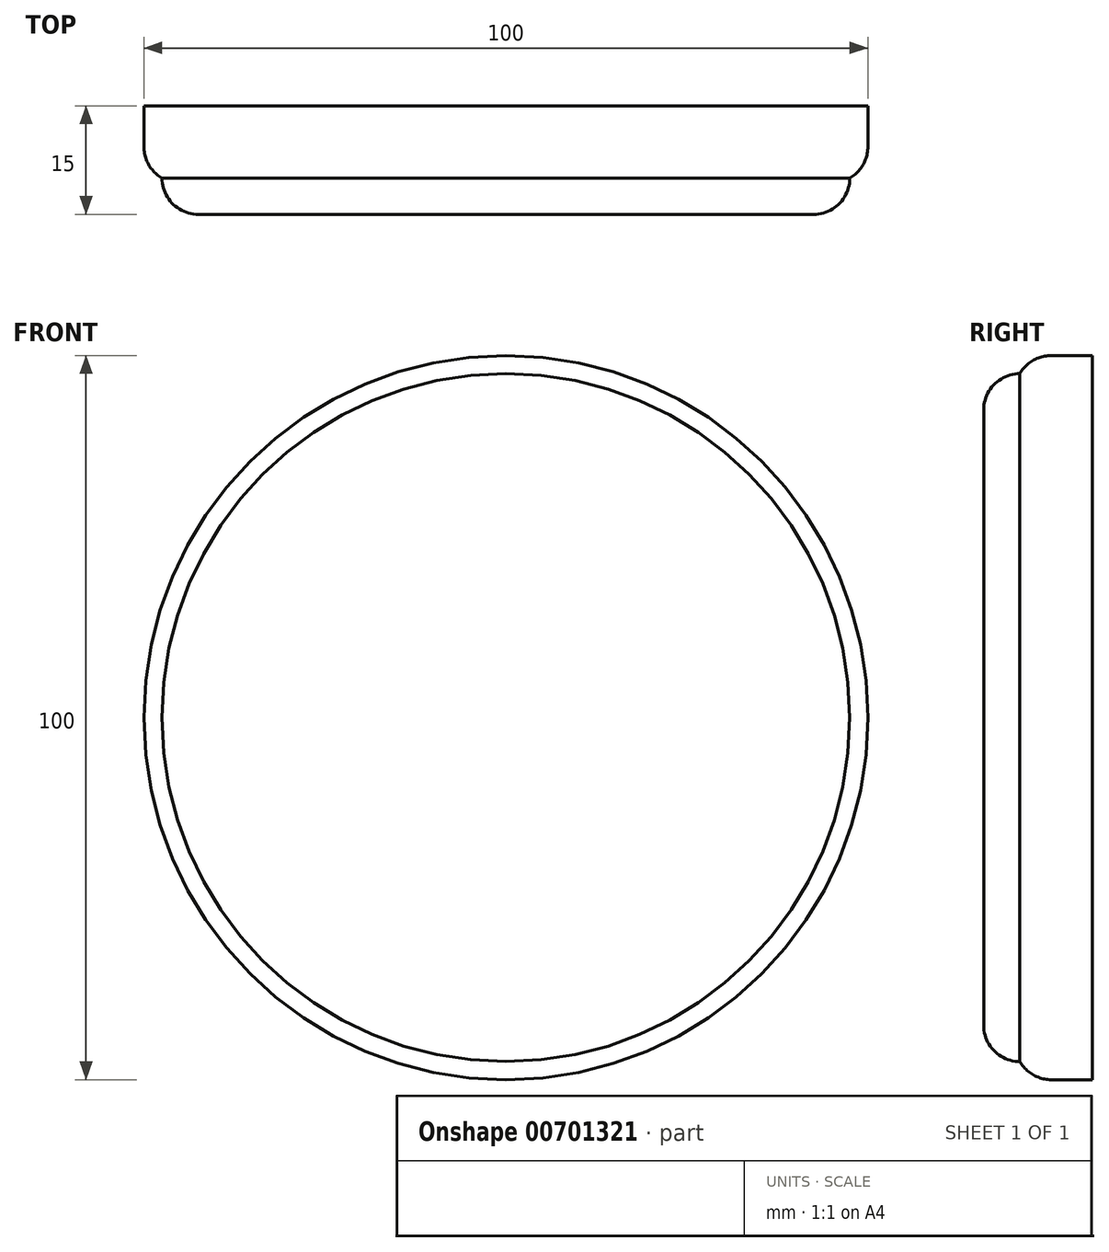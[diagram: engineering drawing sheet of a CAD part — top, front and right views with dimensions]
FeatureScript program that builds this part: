
annotation { "Feature Type Name" : "Feature", "Feature Type Description" : "" }
export const myFeature = defineFeature(function(context is Context, id is Id, definition is map)
    precondition{}
    {
        {
            var Q0;
            Q0=qCreatedBy(makeId("Front.planeOp"),FACE);
            var sketch = newSketch(context, id + "F0", { "sketchPlane" : qUnion([Q0])});
            skCircle(sketch, "E0", {"center": v(0, 0) * mm, "radius": 50 * mm});
            skSolve(sketch);
        }
        {
            var Q0;
            Q0 = qSketchRegion(id + "F0", true);
            extrude(context, id + "F1", {"entities" : qUnion([Q0]), "depth" : 10 * mm, "offsetDistance" : 25 * mm});
        }
        {
            var Q0;
            Q0=makeQuery(id+"F1.opExtrude","CAP_FACE",FACE,{"disambiguationData":[OSD([sQuery(id+"F0.wireOp",EDGE,"E0")])],"isStart":false});
            var sketch = newSketch(context, id + "F2", { "sketchPlane" : qUnion([Q0])});
            skCircle(sketch, "E1", {"center": v(0, 0) * mm, "radius": 47.5 * mm});
            skSolve(sketch);
        }
        {
            var Q0;
            Q0=makeQuery(id+"F2.imprint","IMPRINT",FACE,{"disambiguationData":[TD([[makeQuery(id+"F2.imprint","IMPRINT",EDGE,{"derivedFrom":sQuery(id+"F2.wireOp",EDGE,"E1")}),1.0]])]});
            extrude(context, id + "F3", {"entities" : qUnion([Q0]), "operationType" : NewBodyOperationType.ADD, "depth" : 5 * mm, "offsetDistance" : 25 * mm});
        }
        {
            var Q0;
            Q0=makeQuery(id+"F1.opExtrude","CAP_EDGE",EDGE,{"disambiguationData":[OSD([sQuery(id+"F0.wireOp",EDGE,"E0")])],"isStart":false});
            var Q1;
            Q1=makeQuery(id+"F3.opExtrude","CAP_EDGE",EDGE,{"disambiguationData":[OSD([sQuery(id+"F2.wireOp",EDGE,"E1")])],"isStart":false});
            fillet(context, id + "F4", {"entities" : qUnion([Q0, Q1]), "radius" : 5 * mm, "tangentPropagation" : true, "allowEdgeOverflow" : false});
        }
    });
